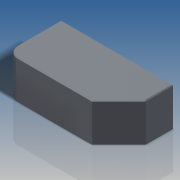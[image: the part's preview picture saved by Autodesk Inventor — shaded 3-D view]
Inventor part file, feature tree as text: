
AUTODESK INVENTOR PART (.ipt)
format: ipt  version: 2016 SP2 (Build 200236200, 236)  size: 117,760 bytes
history: native  units: in
note: dims shown in document units (in); Inventor stores cm internally (conversion verified against a paired STEP export)
features: extrude x1, fillet x1, chamfer x1, sketch x1
ambient origin geometry x8: Origin, YZ Plane, XZ Plane, XY Plane, X Axis, Y Axis, Z Axis, Center Point
bodies: Solid1 (feature_tree)
feature tree (4):
  extrude  "Extrusion1"  Depth=0.6016in
  fillet  "Fillet1"  Radius=0.063in
  chamfer  "Chamfer2"  Distance=0.1433in
  sketch  "Sketch2"  dims[d0=0.2929in d1=0.6016in d2=0.063in d3=0.1433in d4=0.1433in d5=0.2047in d6=0.0in d10=0.0047in d11=0.0047in d12=0.0787in d13=45.0deg]
